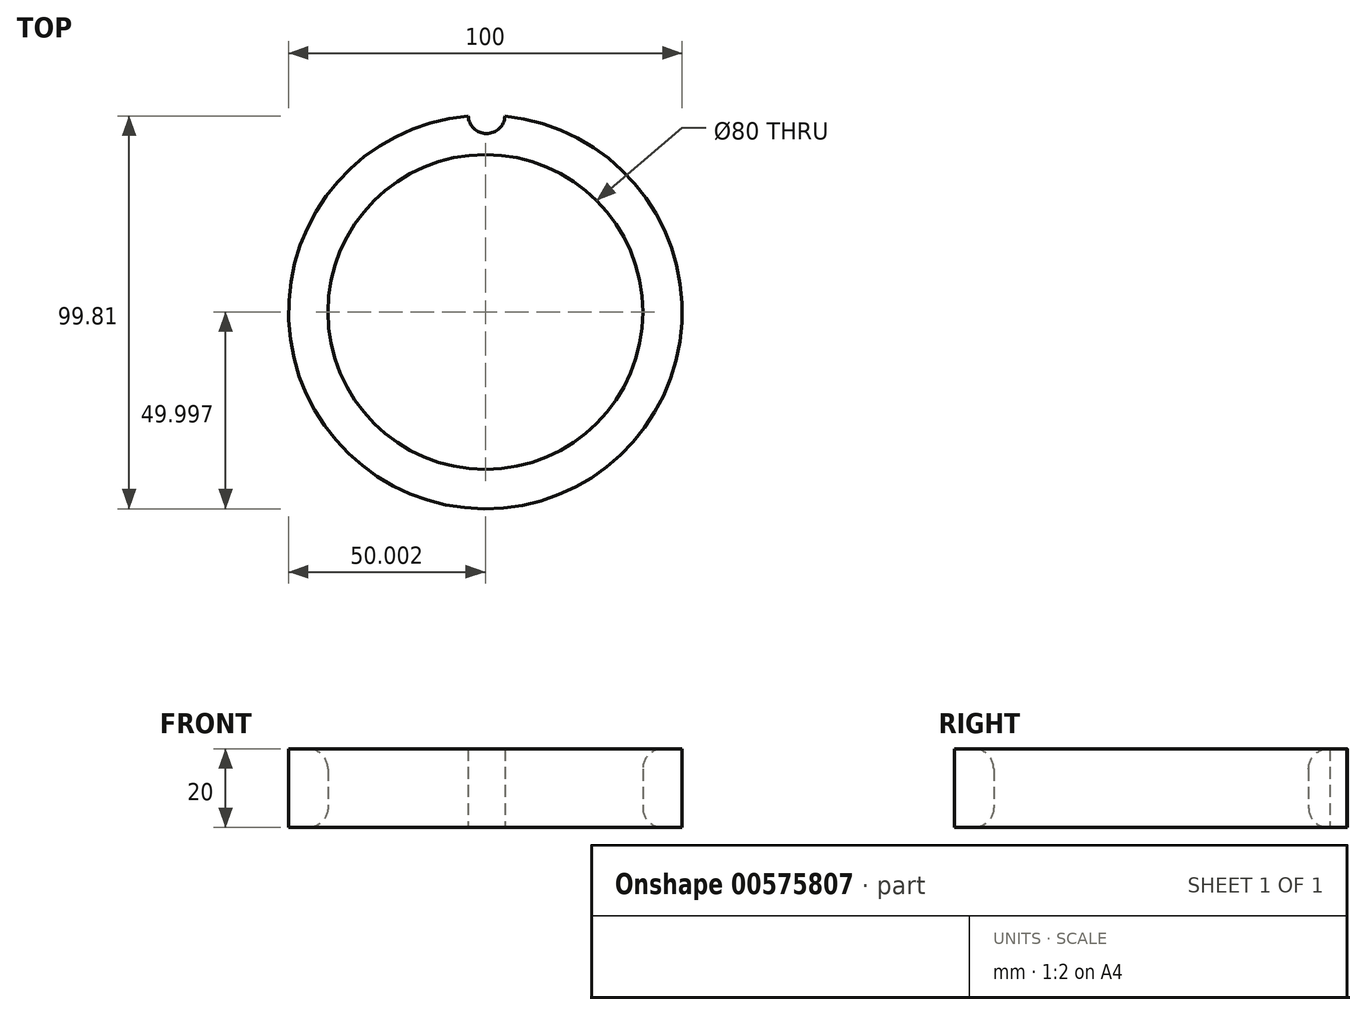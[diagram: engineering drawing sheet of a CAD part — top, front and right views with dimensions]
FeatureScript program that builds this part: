
annotation { "Feature Type Name" : "Feature", "Feature Type Description" : "" }
export const myFeature = defineFeature(function(context is Context, id is Id, definition is map)
    precondition{}
    {
        {
            var Q0;
            Q0=qCreatedBy(makeId("Top.planeOp"),FACE);
            var sketch = newSketch(context, id + "F0", { "sketchPlane" : qUnion([Q0])});
            skCircle(sketch, "E0", {"center": v(-111.1, 46.6) * mm, "radius": 50 * mm});
            skCircle(sketch, "E1", {"center": v(-111.1, 46.6) * mm, "radius": 40 * mm});
            skCircle(sketch, "E2", {"center": v(-110.8, 96.6) * mm, "radius": 4.66 * mm});
            skSolve(sketch);
        }
        {
            var Q0;
            Q0=makeQuery(id+"F0.imprint","IMPRINT",FACE,{"disambiguationData":[TD([[makeQuery(id+"F0.imprint","IMPRINT",EDGE,{"derivedFrom":sQuery(id+"F0.wireOp",EDGE,"E1")}),-1.0]])]});
            extrude(context, id + "F1", {"entities" : qUnion([Q0]), "depth" : 20 * mm, "offsetDistance" : 25.4 * mm});
        }
        {
            var Q0;
            Q0=makeQuery(id+"F1.opExtrude","CAP_EDGE",EDGE,{"disambiguationData":[OSD([sQuery(id+"F0.wireOp",EDGE,"E1")])],"isStart":false});
            fillet(context, id + "F2", {"entities" : qUnion([Q0]), "radius" : 5.08 * mm, "tangentPropagation" : true, "allowEdgeOverflow" : false});
        }
        {
            var Q0;
            Q0=makeQuery(id+"F1.opExtrude","CAP_EDGE",EDGE,{"disambiguationData":[OSD([sQuery(id+"F0.wireOp",EDGE,"E1")])],"isStart":true});
            fillet(context, id + "F3", {"entities" : qUnion([Q0]), "radius" : 5.08 * mm, "tangentPropagation" : true, "allowEdgeOverflow" : false});
        }
    });
